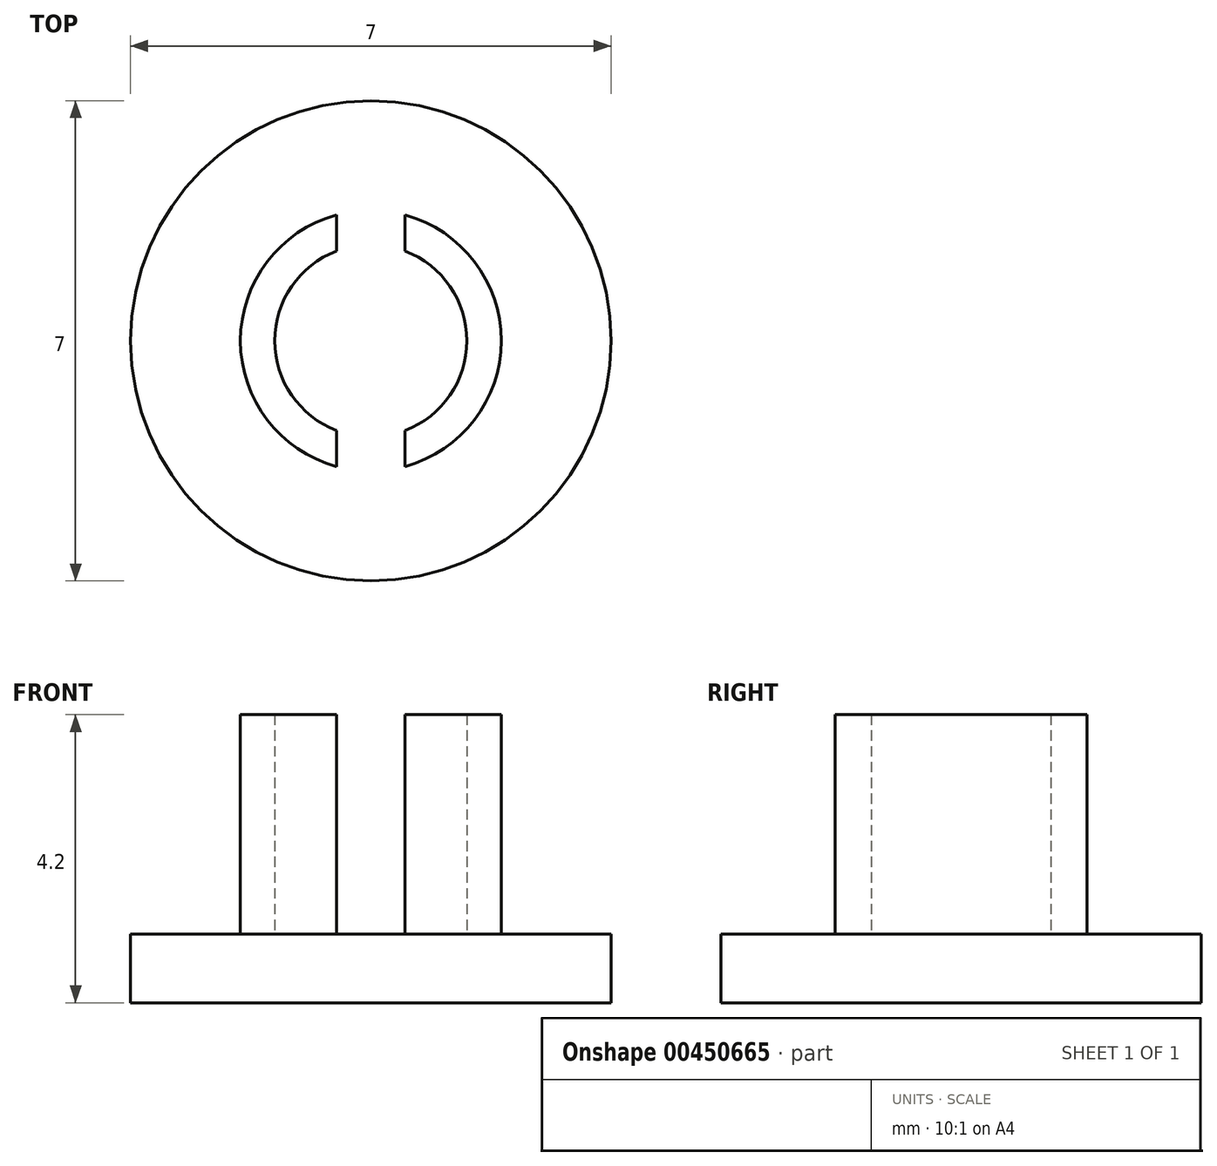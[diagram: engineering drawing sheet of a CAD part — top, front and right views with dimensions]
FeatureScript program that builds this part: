
annotation { "Feature Type Name" : "Feature", "Feature Type Description" : "" }
export const myFeature = defineFeature(function(context is Context, id is Id, definition is map)
    precondition{}
    {
        {
            var Q0;
            Q0=qCreatedBy(makeId("Top.planeOp"),FACE);
            var sketch = newSketch(context, id + "F0", { "sketchPlane" : qUnion([Q0])});
            skCircle(sketch, "E0", {"center": v(0, 0) * mm, "radius": 3.5 * mm});
            skSolve(sketch);
        }
        {
            var Q0;
            Q0=qSketchRegion(id+"F0",true);
            extrude(context, id + "F1", {"entities" : qUnion([Q0]), "endBound" : BoundingType.SYMMETRIC, "depth" : 1 * mm});
        }
        {
            var Q0;
            Q0=makeQuery(id+"F1.opExtrude","CAP_FACE",FACE,{"disambiguationData":[OSD([sQuery(id+"F0.wireOp",EDGE,"E0")])],"isStart":false});
            var sketch = newSketch(context, id + "F2", { "sketchPlane" : qUnion([Q0])});
            skCircle(sketch, "E1", {"center": v(0, 0) * mm, "radius": 1.9 * mm});
            skCircle(sketch, "E2", {"center": v(0, 0) * mm, "radius": 1.4 * mm});
            skSolve(sketch);
        }
        {
            var Q0;
            Q0=qSketchRegion(id+"F2",true);
            extrude(context, id + "F3", {"entities" : qUnion([Q0]), "operationType" : NewBodyOperationType.ADD, "depth" : 3.2 * mm});
        }
        {
            var Q0;
            Q0=makeQuery(id+"F3.opExtrude","CAP_FACE",FACE,{"disambiguationData":[OSD([sQuery(id+"F2.wireOp",EDGE,"E1"),sQuery(id+"F2.wireOp",EDGE,"E2")])],"isStart":false});
            var sketch = newSketch(context, id + "F4", { "sketchPlane" : qUnion([Q0])});
            skLineSegment(sketch, "E3.bottom", {"start": v(-0.5, 2.94) * mm, "end": v(0.5, 2.94) * mm});
            skLineSegment(sketch, "E3.top", {"start": v(-0.5, -3.52) * mm, "end": v(0.5, -3.52) * mm});
            skLineSegment(sketch, "E3.left", {"start": v(-0.5, 2.94) * mm, "end": v(-0.5, -3.52) * mm});
            skLineSegment(sketch, "E3.right", {"start": v(0.5, 2.94) * mm, "end": v(0.5, -3.52) * mm});
            skSolve(sketch);
        }
        {
            var Q0;
            Q0=qSketchRegion(id+"F4",true);
            var Q1;
            {var subQ0=sQuery(id+"F0.wireOp",EDGE,"E0");Q1=makeQuery(id+"F3.boolean.opBoolean","SPLIT",FACE,{"disambiguationData":[TD([makeQuery(id+"F1.opExtrude","SWEPT_FACE",FACE,{"disambiguationData":[OSD([subQ0])]})])],"derivedFrom":makeQuery(id+"F1.opExtrude","CAP_FACE",FACE,{"disambiguationData":[OSD([subQ0])],"isStart":false})});}
            extrude(context, id + "F5", {"entities" : qUnion([Q0]), "operationType" : NewBodyOperationType.REMOVE, "endBound" : BoundingType.UP_TO_SURFACE, "oppositeDirection" : true, "endBoundEntityFace" : qUnion([Q1]), "depth" : 5 * mm});
        }
    });
